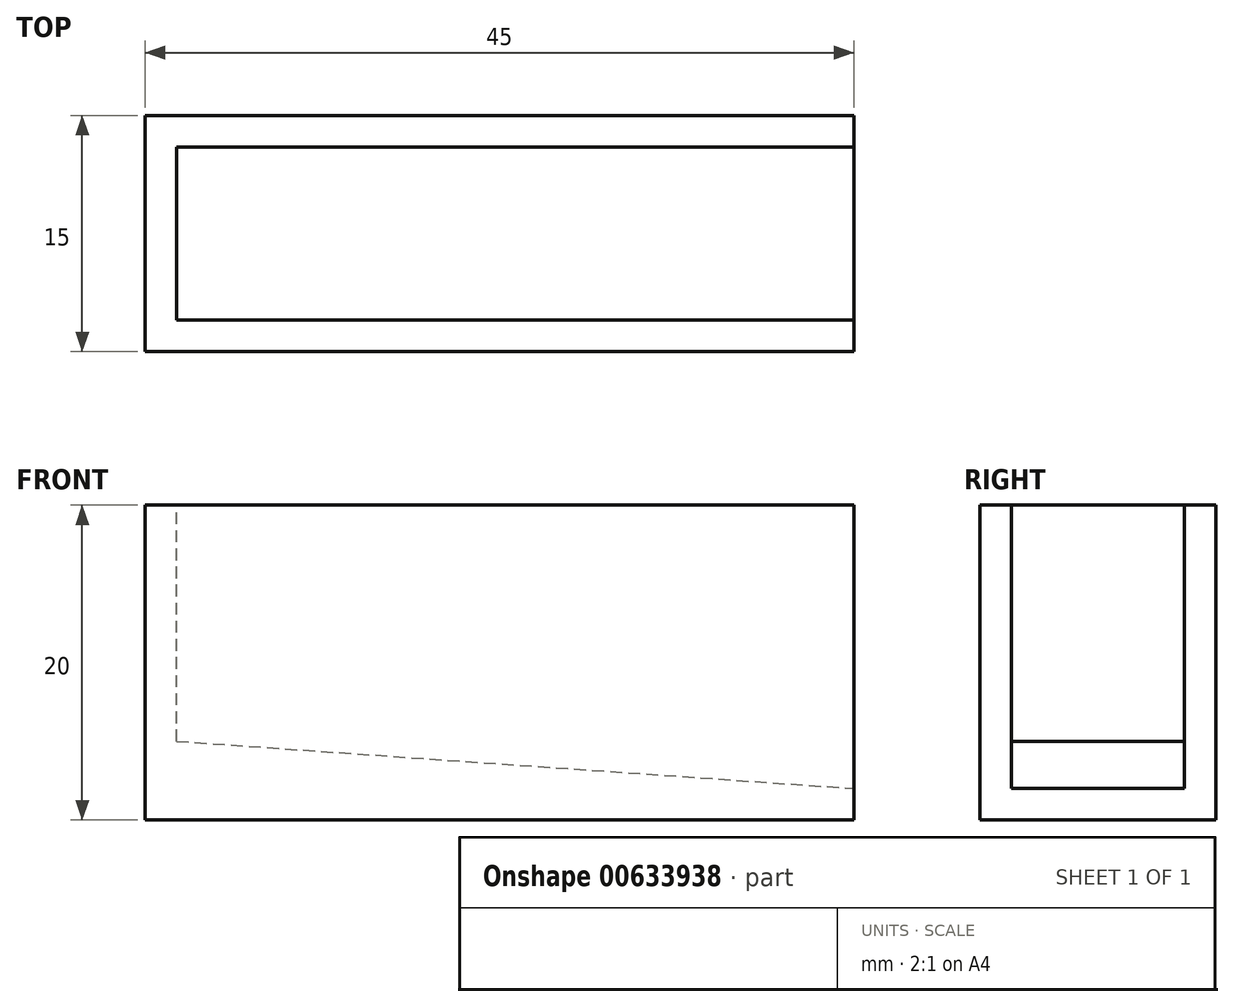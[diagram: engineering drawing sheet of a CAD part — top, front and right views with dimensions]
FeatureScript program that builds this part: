
annotation { "Feature Type Name" : "Feature", "Feature Type Description" : "" }
export const myFeature = defineFeature(function(context is Context, id is Id, definition is map)
    precondition{}
    {
        {
            var Q0;
            Q0=qCreatedBy(makeId("Top.planeOp"),FACE);
            var sketch = newSketch(context, id + "F0", { "sketchPlane" : qUnion([Q0])});
            skLineSegment(sketch, "E0.bottom", {"start": v(-22.5, 7.5) * mm, "end": v(22.5, 7.5) * mm});
            skLineSegment(sketch, "E0.top", {"start": v(-22.5, -7.5) * mm, "end": v(22.5, -7.5) * mm});
            skLineSegment(sketch, "E0.left", {"start": v(-22.5, 7.5) * mm, "end": v(-22.5, -7.5) * mm});
            skLineSegment(sketch, "E0.right", {"start": v(22.5, 7.5) * mm, "end": v(22.5, -7.5) * mm});
            skSolve(sketch);
        }
        {
            var Q0;
            Q0 = qSketchRegion(id + "F0", true);
            extrude(context, id + "F1", {"entities" : qUnion([Q0]), "depth" : 20 * mm, "offsetDistance" : 25 * mm});
        }
        {
            var Q0;
            Q0=makeQuery(id+"F1.opExtrude","CAP_FACE",FACE,{"disambiguationData":[OSD([sQuery(id+"F0.wireOp",EDGE,"E0.bottom"),sQuery(id+"F0.wireOp",EDGE,"E0.top"),sQuery(id+"F0.wireOp",EDGE,"E0.left"),sQuery(id+"F0.wireOp",EDGE,"E0.right")])],"isStart":false});
            var sketch = newSketch(context, id + "F2", { "sketchPlane" : qUnion([Q0])});
            skLineSegment(sketch, "E1", {"start": v(-20.5, 7.5) * mm, "end": v(-20.5, 5.5) * mm, "construction": true});
            skLineSegment(sketch, "E2", {"start": v(-22.5, -5.5) * mm, "end": v(-20.5, -5.5) * mm, "construction": true});
            skLineSegment(sketch, "E3.bottom", {"start": v(-20.5, -5.5) * mm, "end": v(22.5, -5.5) * mm});
            skLineSegment(sketch, "E4", {"start": v(-20.5, -5.5) * mm, "end": v(-20.5, 5.5) * mm});
            skLineSegment(sketch, "E5", {"start": v(-20.5, 5.5) * mm, "end": v(22.5, 5.5) * mm});
            skLineSegment(sketch, "E6", {"start": v(22.5, 5.5) * mm, "end": v(22.5, -5.5) * mm});
            skSolve(sketch);
        }
        {
            var Q0;
            Q0 = qSketchRegion(id + "F2", true);
            extrude(context, id + "F3", {"entities" : qUnion([Q0]), "operationType" : NewBodyOperationType.REMOVE, "oppositeDirection" : true, "depth" : 15 * mm, "offsetDistance" : 25 * mm});
        }
        {
            var Q0;
            Q0=makeQuery(id+"F1.opExtrude","SWEPT_FACE",FACE,{"disambiguationData":[OSD([sQuery(id+"F0.wireOp",EDGE,"E0.top")])]});
            var sketch = newSketch(context, id + "F4", { "sketchPlane" : qUnion([Q0])});
            skLineSegment(sketch, "E7", {"start": v(-22.5, 0) * mm, "end": v(-22.5, 5) * mm, "construction": true});
            skLineSegment(sketch, "E8", {"start": v(-22.5, 0) * mm, "end": v(22.5, 0) * mm, "construction": true});
            skLineSegment(sketch, "E9", {"start": v(22.5, 0) * mm, "end": v(22.5, 2) * mm, "construction": true});
            skLineSegment(sketch, "E10", {"start": v(-22.5, 5) * mm, "end": v(-20.5, 5) * mm, "construction": true});
            skLineSegment(sketch, "E11", {"start": v(-20.5, 5) * mm, "end": v(22.5, 2) * mm});
            skLineSegment(sketch, "E12", {"start": v(-20.5, 5) * mm, "end": v(22.5, 5) * mm});
            skLineSegment(sketch, "E13", {"start": v(22.5, 5) * mm, "end": v(22.5, 2) * mm});
            skSolve(sketch);
        }
        {
            var Q0;
            Q0 = qSketchRegion(id + "F4", true);
            extrude(context, id + "F5", {"entities" : qUnion([Q0]), "operationType" : NewBodyOperationType.REMOVE, "oppositeDirection" : true, "depth" : 13 * mm, "offsetDistance" : 25 * mm, "hasSecondDirection" : true, "secondDirectionOppositeDirection" : true, "secondDirectionDepth" : 2 * mm});
        }
    });
